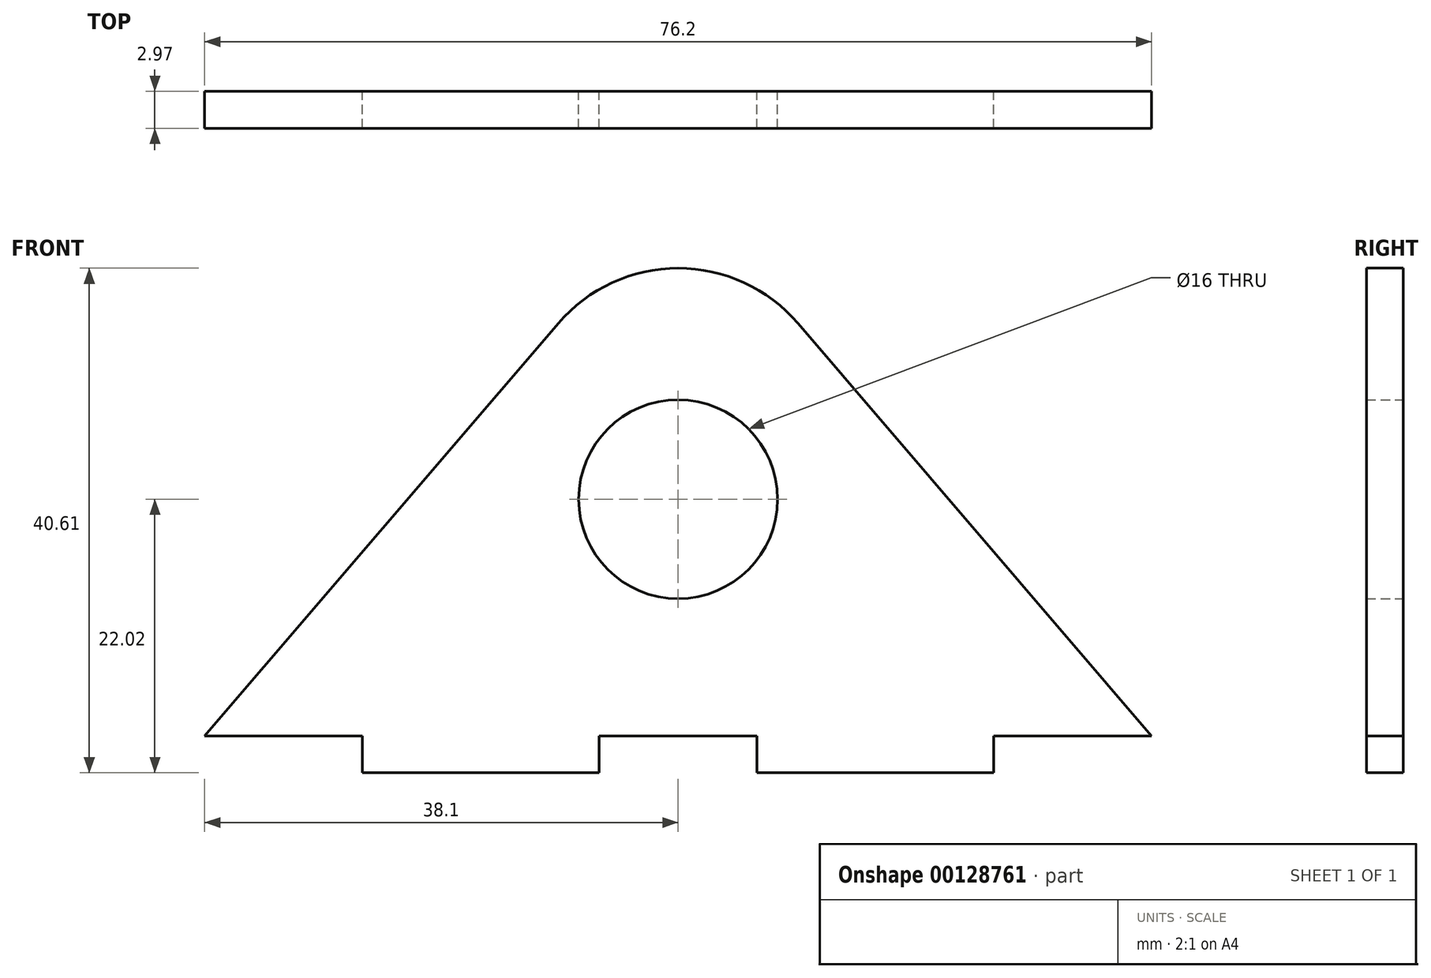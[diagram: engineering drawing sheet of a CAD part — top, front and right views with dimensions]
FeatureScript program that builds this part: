
annotation { "Feature Type Name" : "Feature", "Feature Type Description" : "" }
export const myFeature = defineFeature(function(context is Context, id is Id, definition is map)
    precondition{}
    {
        {
            var Q0;
            Q0=qCreatedBy(makeId("Front.planeOp"),FACE);
            var sketch = newSketch(context, id + "F0", { "sketchPlane" : qUnion([Q0])});
            skLineSegment(sketch, "E0", {"start": v(-25.4, -19.05) * mm, "end": v(-25.4, -22.02) * mm});
            skLineSegment(sketch, "E1", {"start": v(-25.4, -22.02) * mm, "end": v(-6.35, -22.02) * mm});
            skLineSegment(sketch, "E2", {"start": v(-6.35, -22.02) * mm, "end": v(-6.35, -19.05) * mm});
            skLineSegment(sketch, "E3", {"start": v(-6.35, -19.05) * mm, "end": v(6.35, -19.05) * mm});
            skLineSegment(sketch, "E4", {"start": v(6.35, -19.05) * mm, "end": v(6.35, -22.02) * mm});
            skLineSegment(sketch, "E5", {"start": v(6.35, -22.02) * mm, "end": v(25.4, -22.02) * mm});
            skLineSegment(sketch, "E6", {"start": v(25.4, -22.02) * mm, "end": v(25.4, -19.05) * mm});
            skLineSegment(sketch, "E7", {"start": v(-25.4, -19.05) * mm, "end": v(-38.1, -19.05) * mm});
            skLineSegment(sketch, "E8", {"start": v(25.4, -19.05) * mm, "end": v(38.1, -19.05) * mm});
            skPoint(sketch, "E9", {"position": v(0, -19.05) * mm});
            skLineSegment(sketch, "E10", {"start": v(-38.1, -19.05) * mm, "end": v(-9.64, 14.15) * mm});
            skLineSegment(sketch, "E11", {"start": v(9.64, 14.15) * mm, "end": v(38.1, -19.05) * mm});
            skPoint(sketch, "E12.visualSharp", {"position": v(0, 25.4) * mm});
            skArc(sketch, "E12.filletArc", {"start": v(9.64, 14.15) * mm, "mid": v(0, 18.59) * mm, "end": v(-9.64, 14.15) * mm});
            skCircle(sketch, "E13", {"center": v(0, 0) * mm, "radius": 8 * mm});
            skSolve(sketch);
        }
        {
            var Q0;
            Q0=makeQuery(id+"F0.imprint","IMPRINT",FACE,{"disambiguationData":[TD([[makeQuery(id+"F0.imprint","IMPRINT",EDGE,{"derivedFrom":sQuery(id+"F0.wireOp",EDGE,"E0")}),1.0]])]});
            extrude(context, id + "F1", {"entities" : qUnion([Q0]), "depth" : 2.97 * mm});
        }
    });
